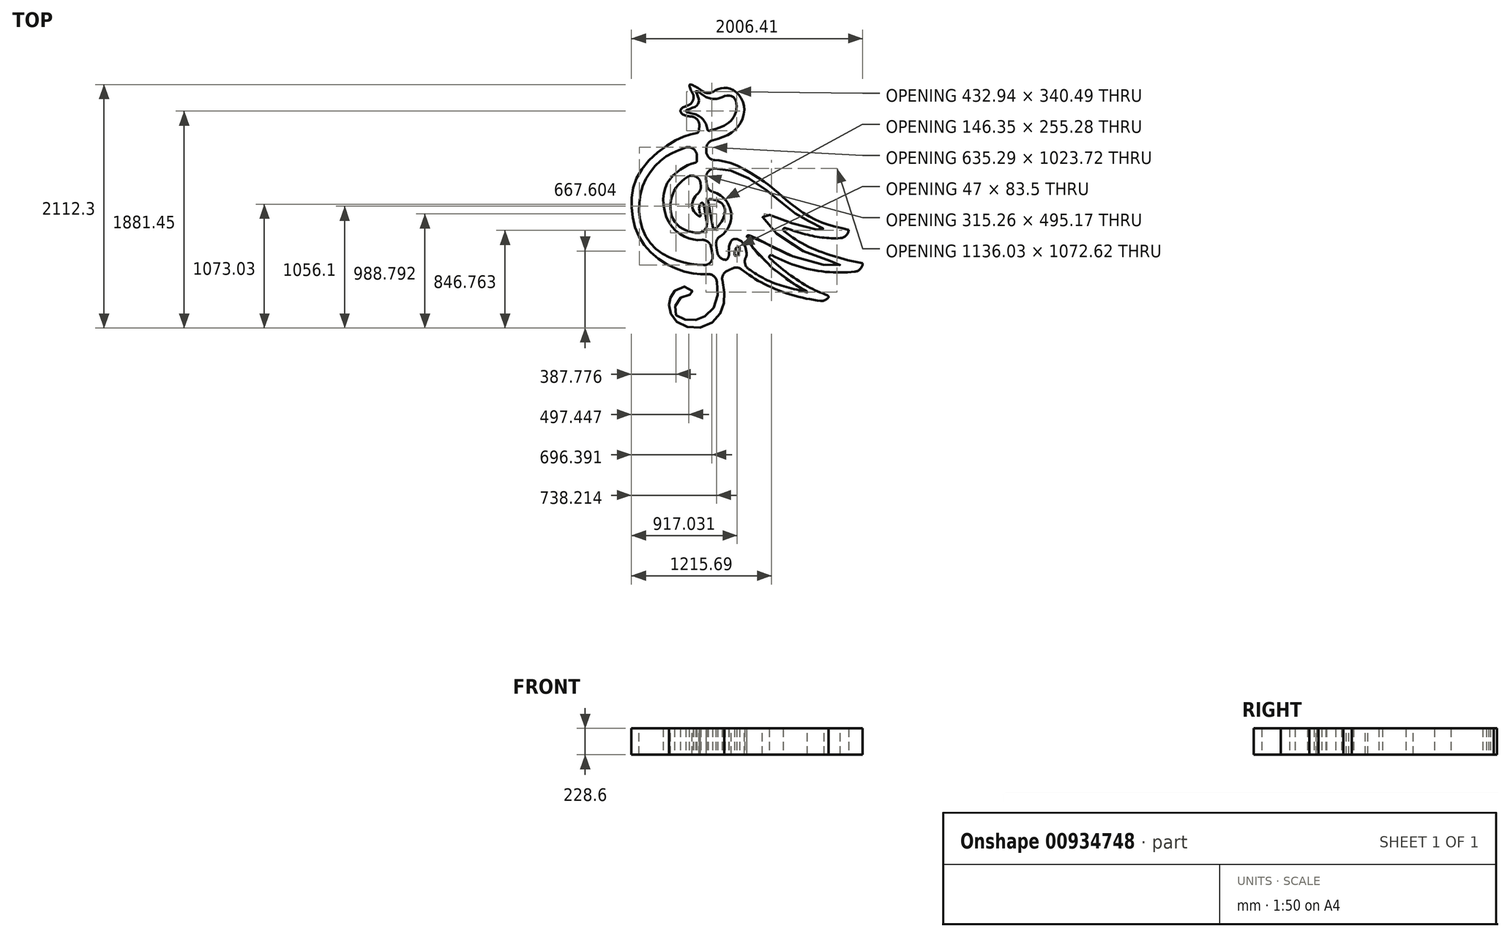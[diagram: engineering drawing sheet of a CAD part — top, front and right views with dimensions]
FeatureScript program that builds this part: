
annotation { "Feature Type Name" : "Feature", "Feature Type Description" : "" }
export const myFeature = defineFeature(function(context is Context, id is Id, definition is map)
    precondition{}
    {
        {
            var Q0;
            Q0=qCreatedBy(makeId("Top.planeOp"),FACE);
            var sketch = newSketch(context, id + "F0", { "sketchPlane" : qUnion([Q0])});
            skFitSpline(sketch, "E0", {"points": [v(-10.13, 34.53) * mm, v(-7.21, 36.28) * mm, v(-3.57, 36.28) * mm, v(0, 32.05) * mm, v(-1.82, 25.06) * mm, v(-10.75, 21.03) * mm], "startDerivative": vector(17.87, 13.15) * mm, "endDerivative": vector(-40.47, -9.18) * mm});
            skLineSegment(sketch, "E1", {"start": v(-10.75, 21.03) * mm, "end": v(-10.75, 15.74) * mm});
            skFitSpline(sketch, "E2", {"points": [v(-10.75, 15.74) * mm, v(-9.04, 15.74) * mm, v(-3.73, 14.85) * mm, v(7.09, 8.67) * mm, v(12.2, 4.3) * mm, v(20.6, -1.41) * mm, v(30.4, -4.44) * mm], "startDerivative": vector(20.65, 0.25) * mm, "endDerivative": vector(50.35, -11.32) * mm});
            skFitSpline(sketch, "E3", {"points": [v(30.4, -4.44) * mm, v(31.48, -5.44) * mm, v(31.42, -6.46) * mm], "startDerivative": vector(2.53, -1.73) * mm, "endDerivative": vector(-0.8, -2.05) * mm});
            skFitSpline(sketch, "E4", {"points": [v(31.42, -6.46) * mm, v(21.27, -6.46) * mm, v(9.3, -3) * mm], "startDerivative": vector(-21.03, -3.5) * mm, "endDerivative": vector(-23.27, 7.73) * mm});
            skFitSpline(sketch, "E5", {"points": [v(9.3, -3) * mm, v(16.48, -8.1) * mm, v(25.06, -11.75) * mm, v(34.46, -14.13) * mm], "startDerivative": vector(21.36, -16.71) * mm, "endDerivative": vector(26.92, -4.42) * mm});
            skFitSpline(sketch, "E6", {"points": [v(34.46, -14.13) * mm, v(35.57, -15.05) * mm, v(35.7, -16.2) * mm], "startDerivative": vector(2.6, -1.56) * mm, "endDerivative": vector(-0.18, -2.61) * mm});
            skFitSpline(sketch, "E7", {"points": [v(35.7, -16.2) * mm, v(25.95, -16.75) * mm, v(14.56, -14.62) * mm, v(5.06, -10.17) * mm], "startDerivative": vector(-29.63, -3.24) * mm, "endDerivative": vector(-27.45, 14.78) * mm});
            skFitSpline(sketch, "E8", {"points": [v(5.06, -10.17) * mm, v(10.3, -15.05) * mm, v(18.4, -20.71) * mm, v(24.86, -23.63) * mm], "startDerivative": vector(15.22, -15.1) * mm, "endDerivative": vector(19.9, -7.85) * mm});
            skFitSpline(sketch, "E9", {"points": [v(24.86, -23.63) * mm, v(25.6, -24.34) * mm, v(25.86, -25.36) * mm], "startDerivative": vector(1.72, -1.28) * mm, "endDerivative": vector(0.3, -2.17) * mm});
            skFitSpline(sketch, "E10", {"points": [v(25.86, -25.36) * mm, v(16.25, -23.9) * mm, v(4.88, -19.52) * mm, v(-1.94, -14.8) * mm], "startDerivative": vector(-28.22, 2.8) * mm, "endDerivative": vector(-20.3, 15.93) * mm});
            skFitSpline(sketch, "E11", {"points": [v(-1.94, -14.8) * mm, v(-4.07, -16.02) * mm, v(-6.53, -16.82) * mm], "startDerivative": vector(-4.2, -2.68) * mm, "endDerivative": vector(-5, -1.36) * mm});
            skFitSpline(sketch, "E12", {"points": [v(-6.53, -16.82) * mm, v(-5.58, -22.99) * mm, v(-6.12, -27.34) * mm, v(-9.82, -31.79) * mm, v(-16.34, -32.55) * mm, v(-20.41, -29.82) * mm, v(-21.58, -26.53) * mm, v(-21.26, -24.33) * mm, v(-19.8, -22.06) * mm, v(-16.12, -21) * mm, v(-14.63, -22.91) * mm, v(-16.73, -23.3) * mm, v(-19.49, -25.89) * mm, v(-19.42, -29.22) * mm, v(-15.27, -30.57) * mm, v(-11.66, -29.72) * mm, v(-7.87, -25.36) * mm, v(-7.8, -18.66) * mm, v(-7.97, -16.82) * mm], "startDerivative": vector(17.62, -92.77) * mm, "endDerivative": vector(-2.9, 39.27) * mm});
            skFitSpline(sketch, "E13", {"points": [v(-7.97, -16.82) * mm, v(-11.92, -17.32) * mm, v(-20.1, -15.42) * mm, v(-28.9, -8.64) * mm, v(-32.39, 1.98) * mm, v(-29.53, 12.97) * mm, v(-18.95, 21.78) * mm, v(-13.06, 23.63) * mm], "startDerivative": vector(-38.08, -8.2) * mm, "endDerivative": vector(45.84, 9.25) * mm});
            skLineSegment(sketch, "E14", {"start": v(-13.06, 23.63) * mm, "end": v(-12.39, 28.22) * mm});
            skFitSpline(sketch, "E15", {"points": [v(-13.01, 32.27) * mm, v(-15.6, 37.51) * mm, v(-10.13, 34.53) * mm], "startDerivative": vector(-9.2, 14.72) * mm, "endDerivative": vector(14.84, -10.07) * mm});
            skFitSpline(sketch, "E16", {"points": [v(-12.39, 28.22) * mm, v(-17.63, 29) * mm, v(-18.11, 30.39) * mm, v(-13.01, 32.27) * mm], "startDerivative": vector(-16.14, 0.23) * mm, "endDerivative": vector(17.28, 3.78) * mm});
            skFitSpline(sketch, "E17", {"points": [v(-11.13, 13.07) * mm, v(-4.51, 12.94) * mm, v(5.07, 8.13) * mm, v(13.22, 1.65) * mm, v(18.4, -1.77) * mm, v(23.3, -4.37) * mm, v(15.18, -2.91) * mm, v(5.48, 0) * mm, v(14.91, -9.33) * mm, v(28, -14.5) * mm, v(16.18, -12.87) * mm, v(1.1, -6.15) * mm, v(9.12, -16.25) * mm, v(18.48, -22.46) * mm, v(8.38, -19.25) * mm], "startDerivative": vector(111.68, 10.83) * mm, "endDerivative": vector(-207.34, 71.55) * mm});
            skFitSpline(sketch, "E18", {"points": [v(18.48, -22.46) * mm, v(7.51, -19.32) * mm, v(-0.84, -14.12) * mm], "startDerivative": vector(-22.14, 4.82) * mm, "endDerivative": vector(-16.43, 11.95) * mm});
            skFitSpline(sketch, "E19", {"points": [v(-0.84, -14.12) * mm, v(0.6, -12.65) * mm, v(0.59, -9.6) * mm, v(-1.32, -7.34) * mm, v(-3.45, -7.55) * mm, v(-4.2, -10.99) * mm, v(-3.45, -12.62) * mm], "startDerivative": vector(11.39, 8.05) * mm, "endDerivative": vector(6.68, -9.48) * mm});
            skLineSegment(sketch, "E20", {"start": v(-3.45, -12.62) * mm, "end": v(-7.02, -14.28) * mm});
            skLineSegment(sketch, "E21", {"start": v(-7.02, -14.28) * mm, "end": v(-8.25, -6.85) * mm});
            skFitSpline(sketch, "E22", {"points": [v(-1.3, -9.18) * mm, v(-2.5, -10.5) * mm, v(-2.38, -11.97) * mm, v(-1.29, -10.94) * mm, v(-1.3, -9.18) * mm]});
            skLineSegment(sketch, "E23", {"start": v(-11.13, 13.07) * mm, "end": v(-10.41, 6.9) * mm});
            skFitSpline(sketch, "E24", {"points": [v(-10.41, 6.9) * mm, v(-6.43, 5.3) * mm, v(-3.53, 0) * mm, v(-5.67, -5.52) * mm, v(-8.25, -6.85) * mm], "startDerivative": vector(17.17, -4.04) * mm, "endDerivative": vector(-13.43, -4.01) * mm});
            skLineSegment(sketch, "E25", {"start": v(-13.46, 20.4) * mm, "end": v(-13.46, 15.12) * mm});
            skLineSegment(sketch, "E26", {"start": v(-12.9, 12.8) * mm, "end": v(-12.13, 6.7) * mm});
            skLineSegment(sketch, "E27", {"start": v(-11.64, 3.88) * mm, "end": v(-10.22, -4.8) * mm});
            skLineSegment(sketch, "E28", {"start": v(-9.84, -7.12) * mm, "end": v(-8.36, -14.68) * mm});
            skLineSegment(sketch, "E29", {"start": v(-10.35, 4.3) * mm, "end": v(-8.65, -4.54) * mm});
            skFitSpline(sketch, "E30", {"points": [v(-10.35, 4.3) * mm, v(-7.54, 3.94) * mm, v(-5.43, 1.87) * mm, v(-6.37, -2.14) * mm, v(-8.65, -4.54) * mm], "startDerivative": vector(13.48, 2.7) * mm, "endDerivative": vector(-9.9, -7.5) * mm});
            skFitSpline(sketch, "E31", {"points": [v(-10.22, -4.8) * mm, v(-13.77, -5.29) * mm, v(-19.92, -2.13) * mm, v(-20.51, 5.76) * mm, v(-16.7, 10.53) * mm, v(-12.9, 12.8) * mm], "startDerivative": vector(-19.94, -5.82) * mm, "endDerivative": vector(21.4, 11.25) * mm});
            skFitSpline(sketch, "E32", {"points": [v(-9.84, -7.12) * mm, v(-15.2, -7.12) * mm, v(-21.65, -2.14) * mm, v(-22.66, 7.61) * mm, v(-18.38, 12.9) * mm, v(-13.46, 15.12) * mm], "startDerivative": vector(-29.72, -3.95) * mm, "endDerivative": vector(28.59, 4.89) * mm});
            skFitSpline(sketch, "E33", {"points": [v(-13.46, 20.4) * mm, v(-22.96, 16.34) * mm, v(-29.72, 6.27) * mm, v(-27.32, -7.8) * mm, v(-16.73, -14.02) * mm, v(-8.36, -14.68) * mm], "startDerivative": vector(-54.3, -17.43) * mm, "endDerivative": vector(46.52, 1.31) * mm});
            skFitSpline(sketch, "E34", {"points": [v(-11.64, 3.88) * mm, v(-12.86, 1.87) * mm, v(-12.45, -0.54) * mm, v(-14.45, 1.05) * mm, v(-14.45, 4.38) * mm, v(-12.13, 6.7) * mm], "startDerivative": vector(-9.9, -9.04) * mm, "endDerivative": vector(15.08, 6.28) * mm});
            skLineSegment(sketch, "E35", {"start": v(-12.54, 34.42) * mm, "end": v(-8.5, 32.11) * mm});
            skLineSegment(sketch, "E36", {"start": v(-12.54, 34.42) * mm, "end": v(-10.37, 30.67) * mm});
            skLineSegment(sketch, "E37", {"start": v(-10.37, 30.67) * mm, "end": v(-12.25, 30.1) * mm});
            skLineSegment(sketch, "E38", {"start": v(-12.25, 30.1) * mm, "end": v(-9.99, 28.4) * mm});
            skLineSegment(sketch, "E39", {"start": v(-9.99, 28.4) * mm, "end": v(-10.56, 24.03) * mm});
            skFitSpline(sketch, "E40", {"points": [v(-10.56, 24.03) * mm, v(-5.03, 26) * mm, v(-2.38, 29.08) * mm, v(-2.48, 33.36) * mm, v(-5.03, 34.37) * mm, v(-8.5, 32.11) * mm], "startDerivative": vector(25.42, 6.86) * mm, "endDerivative": vector(-17, -15.34) * mm});
            skLineSegment(sketch, "E41", {"start": v(-36.5, 0) * mm, "end": v(39.7, 0) * mm, "construction": true});
            skSolve(sketch);
        }
        {
            var Q0;
            Q0 = qSketchRegion(id + "F0", true);
            extrude(context, id + "F1", {"entities" : qUnion([Q0]), "depth" : 7.62 * mm, "offsetDistance" : 25.4 * mm});
        }
        {
            var Q0;
            Q0=makeQuery(id+"F1.opExtrude","SWEPT_EDGE",EDGE,{"disambiguationData":[OSD([sQuery(id+"F0.wireOp",EDGE,"E0"),sQuery(id+"F0.wireOp",EDGE,"E1")])]});
            var Q1;
            Q1=makeQuery(id+"F1.opExtrude","SWEPT_EDGE",EDGE,{"disambiguationData":[OSD([sQuery(id+"F0.wireOp",EDGE,"E1"),sQuery(id+"F0.wireOp",EDGE,"E2")])]});
            var Q2;
            Q2=makeQuery(id+"F1.opExtrude","SWEPT_EDGE",EDGE,{"disambiguationData":[OSD([sQuery(id+"F0.wireOp",EDGE,"E3"),sQuery(id+"F0.wireOp",EDGE,"E4")])]});
            var Q3;
            Q3=makeQuery(id+"F1.opExtrude","SWEPT_EDGE",EDGE,{"disambiguationData":[OSD([sQuery(id+"F0.wireOp",EDGE,"E6"),sQuery(id+"F0.wireOp",EDGE,"E7")])]});
            var Q4;
            Q4=makeQuery(id+"F1.opExtrude","SWEPT_EDGE",EDGE,{"disambiguationData":[OSD([sQuery(id+"F0.wireOp",EDGE,"E9"),sQuery(id+"F0.wireOp",EDGE,"E10")])]});
            var Q5;
            Q5=makeQuery(id+"F1.opExtrude","SWEPT_EDGE",EDGE,{"disambiguationData":[OSD([sQuery(id+"F0.wireOp",EDGE,"E11"),sQuery(id+"F0.wireOp",EDGE,"E12")])]});
            var Q6;
            Q6=makeQuery(id+"F1.opExtrude","SWEPT_EDGE",EDGE,{"disambiguationData":[OSD([sQuery(id+"F0.wireOp",EDGE,"E10"),sQuery(id+"F0.wireOp",EDGE,"E11")])]});
            var Q7;
            Q7=makeQuery(id+"F1.opExtrude","SWEPT_EDGE",EDGE,{"disambiguationData":[OSD([sQuery(id+"F0.wireOp",EDGE,"E18"),sQuery(id+"F0.wireOp",EDGE,"E19")])]});
            var Q8;
            Q8=makeQuery(id+"F1.opExtrude","SWEPT_EDGE",EDGE,{"disambiguationData":[OSD([sQuery(id+"F0.wireOp",EDGE,"E20"),sQuery(id+"F0.wireOp",EDGE,"E21")])]});
            var Q9;
            Q9=makeQuery(id+"F1.opExtrude","SWEPT_EDGE",EDGE,{"disambiguationData":[OSD([sQuery(id+"F0.wireOp",EDGE,"E19"),sQuery(id+"F0.wireOp",EDGE,"E20")])]});
            var Q10;
            Q10=makeQuery(id+"F1.opExtrude","SWEPT_EDGE",EDGE,{"disambiguationData":[OSD([sQuery(id+"F0.wireOp",EDGE,"E21"),sQuery(id+"F0.wireOp",EDGE,"E24")])]});
            var Q11;
            Q11=makeQuery(id+"F1.opExtrude","SWEPT_EDGE",EDGE,{"disambiguationData":[OSD([sQuery(id+"F0.wireOp",EDGE,"E12"),sQuery(id+"F0.wireOp",EDGE,"E13")])]});
            var Q12;
            Q12=makeQuery(id+"F1.opExtrude","SWEPT_EDGE",EDGE,{"disambiguationData":[OSD([sQuery(id+"F0.wireOp",EDGE,"E28"),sQuery(id+"F0.wireOp",EDGE,"E32")])]});
            var Q13;
            Q13=makeQuery(id+"F1.opExtrude","SWEPT_EDGE",EDGE,{"disambiguationData":[OSD([sQuery(id+"F0.wireOp",EDGE,"E28"),sQuery(id+"F0.wireOp",EDGE,"E33")])]});
            var Q14;
            Q14=makeQuery(id+"F1.opExtrude","SWEPT_EDGE",EDGE,{"disambiguationData":[OSD([sQuery(id+"F0.wireOp",EDGE,"E17"),sQuery(id+"F0.wireOp",EDGE,"E23")])]});
            var Q15;
            Q15=makeQuery(id+"F1.opExtrude","SWEPT_EDGE",EDGE,{"disambiguationData":[OSD([sQuery(id+"F0.wireOp",EDGE,"E26"),sQuery(id+"F0.wireOp",EDGE,"E31")])]});
            var Q16;
            Q16=makeQuery(id+"F1.opExtrude","SWEPT_EDGE",EDGE,{"disambiguationData":[OSD([sQuery(id+"F0.wireOp",EDGE,"E25"),sQuery(id+"F0.wireOp",EDGE,"E33")])]});
            var Q17;
            Q17=makeQuery(id+"F1.opExtrude","SWEPT_EDGE",EDGE,{"disambiguationData":[OSD([sQuery(id+"F0.wireOp",EDGE,"E14"),sQuery(id+"F0.wireOp",EDGE,"E16")])]});
            var Q18;
            Q18=makeQuery(id+"F1.opExtrude","SWEPT_EDGE",EDGE,{"disambiguationData":[OSD([sQuery(id+"F0.wireOp",EDGE,"E15"),sQuery(id+"F0.wireOp",EDGE,"E16")])]});
            var Q19;
            Q19=makeQuery(id+"F1.opExtrude","SWEPT_EDGE",EDGE,{"disambiguationData":[OSD([sQuery(id+"F0.wireOp",EDGE,"E0"),sQuery(id+"F0.wireOp",EDGE,"E15")])]});
            var Q20;
            Q20=makeQuery(id+"F1.opExtrude","SWEPT_EDGE",EDGE,{"disambiguationData":[OSD([sQuery(id+"F0.wireOp",EDGE,"E27"),sQuery(id+"F0.wireOp",EDGE,"E31")])]});
            var Q21;
            Q21=makeQuery(id+"F1.opExtrude","SWEPT_EDGE",EDGE,{"disambiguationData":[OSD([sQuery(id+"F0.wireOp",EDGE,"E26"),sQuery(id+"F0.wireOp",EDGE,"E34")])]});
            var Q22;
            Q22=makeQuery(id+"F1.opExtrude","SWEPT_EDGE",EDGE,{"disambiguationData":[OSD([sQuery(id+"F0.wireOp",EDGE,"E23"),sQuery(id+"F0.wireOp",EDGE,"E24")])]});
            fillet(context, id + "F2", {"entities" : qUnion([Q0, Q1, Q2, Q3, Q4, Q5, Q6, Q7, Q8, Q9, Q10, Q11, Q12, Q13, Q14, Q15, Q16, Q17, Q18, Q19, Q20, Q21, Q22]), "radius" : 2.54 * mm, "tangentPropagation" : true, "allowEdgeOverflow" : false});
        }
        {
            var Q0;
            Q0=makeQuery(id+"F1.opExtrude","SWEPT_EDGE",EDGE,{"disambiguationData":[OSD([sQuery(id+"F0.wireOp",EDGE,"E35"),sQuery(id+"F0.wireOp",EDGE,"E40")])]});
            var Q1;
            Q1=makeQuery(id+"F1.opExtrude","SWEPT_EDGE",EDGE,{"disambiguationData":[OSD([sQuery(id+"F0.wireOp",EDGE,"E35"),sQuery(id+"F0.wireOp",EDGE,"E36")])]});
            var Q2;
            Q2=makeQuery(id+"F1.opExtrude","SWEPT_EDGE",EDGE,{"disambiguationData":[OSD([sQuery(id+"F0.wireOp",EDGE,"E36"),sQuery(id+"F0.wireOp",EDGE,"E37")])]});
            var Q3;
            Q3=makeQuery(id+"F1.opExtrude","SWEPT_EDGE",EDGE,{"disambiguationData":[OSD([sQuery(id+"F0.wireOp",EDGE,"E37"),sQuery(id+"F0.wireOp",EDGE,"E38")])]});
            var Q4;
            Q4=makeQuery(id+"F1.opExtrude","SWEPT_EDGE",EDGE,{"disambiguationData":[OSD([sQuery(id+"F0.wireOp",EDGE,"E38"),sQuery(id+"F0.wireOp",EDGE,"E39")])]});
            var Q5;
            Q5=makeQuery(id+"F1.opExtrude","SWEPT_EDGE",EDGE,{"disambiguationData":[OSD([sQuery(id+"F0.wireOp",EDGE,"E39"),sQuery(id+"F0.wireOp",EDGE,"E40")])]});
            var Q6;
            Q6=makeQuery(id+"F1.opExtrude","SWEPT_EDGE",EDGE,{"disambiguationData":[OSD([sQuery(id+"F0.wireOp",EDGE,"E13"),sQuery(id+"F0.wireOp",EDGE,"E14")])]});
            var Q7;
            Q7=makeQuery(id+"F1.opExtrude","SWEPT_EDGE",EDGE,{"disambiguationData":[OSD([sQuery(id+"F0.wireOp",EDGE,"E25"),sQuery(id+"F0.wireOp",EDGE,"E32")])]});
            var Q8;
            Q8=makeQuery(id+"F1.opExtrude","SWEPT_EDGE",EDGE,{"disambiguationData":[OSD([sQuery(id+"F0.wireOp",EDGE,"E27"),sQuery(id+"F0.wireOp",EDGE,"E34")])]});
            var Q9;
            {var subQ0=sQuery(id+"F0.wireOp",EDGE,"E30");var subQ1=sQuery(id+"F0.wireOp",EDGE,"E29");Q9=makeQuery(id+"F1.opExtrude","SWEPT_EDGE",EDGE,{"disambiguationData":[OSD([subQ1,subQ0]),TDD([makeQuery(id+"F0.imprint","INTERSECT",VERTEX,{"disambiguationData":[OD(0.0)],"derivedFrom":[subQ1,subQ0]})])]});}
            var Q10;
            {var subQ0=sQuery(id+"F0.wireOp",EDGE,"E30");var subQ1=sQuery(id+"F0.wireOp",EDGE,"E29");Q10=makeQuery(id+"F1.opExtrude","SWEPT_EDGE",EDGE,{"disambiguationData":[OSD([subQ1,subQ0]),TDD([makeQuery(id+"F0.imprint","INTERSECT",VERTEX,{"disambiguationData":[OD(1.0)],"derivedFrom":[subQ1,subQ0]})])]});}
            var Q11;
            Q11=makeQuery(id+"F1.opExtrude","SWEPT_EDGE",EDGE,{"disambiguationData":[OSD([sQuery(id+"F0.wireOp",EDGE,"E4"),sQuery(id+"F0.wireOp",EDGE,"E5")])]});
            var Q12;
            Q12=makeQuery(id+"F1.opExtrude","SWEPT_EDGE",EDGE,{"disambiguationData":[OSD([sQuery(id+"F0.wireOp",EDGE,"E7"),sQuery(id+"F0.wireOp",EDGE,"E8")])]});
            var Q13;
            Q13=makeQuery(id+"F2.opFillet","BLEND_EDGE",EDGE,{"blendedFrom":[makeQuery(id+"F1.opExtrude","SWEPT_EDGE",EDGE,{"disambiguationData":[OSD([sQuery(id+"F0.wireOp",EDGE,"E9"),sQuery(id+"F0.wireOp",EDGE,"E10")])]}),makeQuery(id+"F1.opExtrude","SWEPT_FACE",FACE,{"disambiguationData":[OSD([sQuery(id+"F0.wireOp",EDGE,"E8")])]})],"blendedInto":[makeQuery(id+"F1.opExtrude","SWEPT_FACE",FACE,{"disambiguationData":[OSD([sQuery(id+"F0.wireOp",EDGE,"E8")])]})]});
            var Q14;
            Q14=makeQuery(id+"F1.opExtrude","SWEPT_EDGE",EDGE,{"disambiguationData":[OSD([sQuery(id+"F0.wireOp",EDGE,"E17"),sQuery(id+"F0.wireOp",EDGE,"E18")])]});
            var Q15;
            {var subQ0=sQuery(id+"F0.wireOp",EDGE,"E20");Q15=makeQuery(id+"F2.opFillet","BLEND_EDGE",EDGE,{"blendedFrom":[makeQuery(id+"F1.opExtrude","SWEPT_EDGE",EDGE,{"disambiguationData":[OSD([sQuery(id+"F0.wireOp",EDGE,"E19"),subQ0])]}),makeQuery(id+"F1.opExtrude","SWEPT_EDGE",EDGE,{"disambiguationData":[OSD([subQ0,sQuery(id+"F0.wireOp",EDGE,"E21")])]})],"blendedInto":[]});}
            fillet(context, id + "F3", {"entities" : qUnion([Q0, Q1, Q2, Q3, Q4, Q5, Q6, Q7, Q8, Q9, Q10, Q11, Q12, Q13, Q14, Q15]), "radius" : 0.5 * mm, "tangentPropagation" : true, "allowEdgeOverflow" : false});
        }
        {
            var Q0;
            Q0=makeQuery(id+"F1.opExtrude","CAP_FACE",FACE,{"disambiguationData":[OSD([sQuery(id+"F0.wireOp",EDGE,"E0"),sQuery(id+"F0.wireOp",EDGE,"E1"),sQuery(id+"F0.wireOp",EDGE,"E2"),sQuery(id+"F0.wireOp",EDGE,"E3"),sQuery(id+"F0.wireOp",EDGE,"E4"),sQuery(id+"F0.wireOp",EDGE,"E5"),sQuery(id+"F0.wireOp",EDGE,"E6"),sQuery(id+"F0.wireOp",EDGE,"E7"),sQuery(id+"F0.wireOp",EDGE,"E8"),sQuery(id+"F0.wireOp",EDGE,"E9"),sQuery(id+"F0.wireOp",EDGE,"E10"),sQuery(id+"F0.wireOp",EDGE,"E11"),sQuery(id+"F0.wireOp",EDGE,"E12"),sQuery(id+"F0.wireOp",EDGE,"E13"),sQuery(id+"F0.wireOp",EDGE,"E14"),sQuery(id+"F0.wireOp",EDGE,"E15"),sQuery(id+"F0.wireOp",EDGE,"E16"),sQuery(id+"F0.wireOp",EDGE,"E17"),sQuery(id+"F0.wireOp",EDGE,"E18"),sQuery(id+"F0.wireOp",EDGE,"E19"),sQuery(id+"F0.wireOp",EDGE,"E20"),sQuery(id+"F0.wireOp",EDGE,"E21"),sQuery(id+"F0.wireOp",EDGE,"E22"),sQuery(id+"F0.wireOp",EDGE,"E23"),sQuery(id+"F0.wireOp",EDGE,"E24"),sQuery(id+"F0.wireOp",EDGE,"E25"),sQuery(id+"F0.wireOp",EDGE,"E26"),sQuery(id+"F0.wireOp",EDGE,"E27"),sQuery(id+"F0.wireOp",EDGE,"E28"),sQuery(id+"F0.wireOp",EDGE,"E29"),sQuery(id+"F0.wireOp",EDGE,"E30"),sQuery(id+"F0.wireOp",EDGE,"E31"),sQuery(id+"F0.wireOp",EDGE,"E32"),sQuery(id+"F0.wireOp",EDGE,"E33"),sQuery(id+"F0.wireOp",EDGE,"E34"),sQuery(id+"F0.wireOp",EDGE,"E35"),sQuery(id+"F0.wireOp",EDGE,"E36"),sQuery(id+"F0.wireOp",EDGE,"E37"),sQuery(id+"F0.wireOp",EDGE,"E38"),sQuery(id+"F0.wireOp",EDGE,"E39"),sQuery(id+"F0.wireOp",EDGE,"E40")])],"isStart":false});
            var sketch = newSketch(context, id + "F4", { "sketchPlane" : qUnion([Q0])});
            skFitSpline(sketch, "E42", {"points": [v(-8.81, 32.3) * mm, v(-13.75, 35.61) * mm, v(-12.99, 33.57) * mm, v(-13.89, 31.24) * mm, v(-16.63, 29.94) * mm, v(-10.02, 28.11) * mm], "startDerivative": vector(-26.98, 22.72) * mm, "endDerivative": vector(33.51, -7.9) * mm});
            skLineSegment(sketch, "E43", {"start": v(-10.02, 28.11) * mm, "end": v(-8.81, 32.3) * mm});
            skSolve(sketch);
        }
        {
            var Q0;
            Q0 = qSketchRegion(id + "F4", true);
            extrude(context, id + "F5", {"entities" : qUnion([Q0]), "operationType" : NewBodyOperationType.REMOVE, "oppositeDirection" : true, "depth" : 25.4 * mm, "offsetDistance" : 25.4 * mm});
        }
        {
            var Q0;
            {var subQ0=sQuery(id+"F4.wireOp",EDGE,"E43");var subQ1=sQuery(id+"F4.wireOp",EDGE,"E42");var subQ2=sQuery(id+"F0.wireOp",EDGE,"E39");var subQ3=sQuery(id+"F0.wireOp",EDGE,"E40");var subQ4=sQuery(id+"F0.wireOp",EDGE,"E38");var subQ5=sQuery(id+"F0.wireOp",EDGE,"E37");var subQ6=sQuery(id+"F0.wireOp",EDGE,"E36");var subQ7=sQuery(id+"F0.wireOp",EDGE,"E35");var subQ8=sQuery(id+"F0.wireOp",EDGE,"E34");var subQ9=sQuery(id+"F0.wireOp",EDGE,"E33");var subQ10=sQuery(id+"F0.wireOp",EDGE,"E32");var subQ11=sQuery(id+"F0.wireOp",EDGE,"E31");var subQ12=sQuery(id+"F0.wireOp",EDGE,"E30");var subQ13=sQuery(id+"F0.wireOp",EDGE,"E29");var subQ14=sQuery(id+"F0.wireOp",EDGE,"E28");var subQ15=sQuery(id+"F0.wireOp",EDGE,"E27");var subQ16=sQuery(id+"F0.wireOp",EDGE,"E26");var subQ17=sQuery(id+"F0.wireOp",EDGE,"E25");var subQ18=sQuery(id+"F0.wireOp",EDGE,"E24");var subQ19=sQuery(id+"F0.wireOp",EDGE,"E23");var subQ20=sQuery(id+"F0.wireOp",EDGE,"E22");var subQ21=sQuery(id+"F0.wireOp",EDGE,"E21");var subQ22=sQuery(id+"F0.wireOp",EDGE,"E20");var subQ23=sQuery(id+"F0.wireOp",EDGE,"E19");var subQ24=sQuery(id+"F0.wireOp",EDGE,"E18");var subQ25=sQuery(id+"F0.wireOp",EDGE,"E17");var subQ26=sQuery(id+"F0.wireOp",EDGE,"E16");var subQ27=sQuery(id+"F0.wireOp",EDGE,"E15");var subQ28=sQuery(id+"F0.wireOp",EDGE,"E14");var subQ29=sQuery(id+"F0.wireOp",EDGE,"E13");var subQ30=sQuery(id+"F0.wireOp",EDGE,"E12");var subQ31=sQuery(id+"F0.wireOp",EDGE,"E11");var subQ32=sQuery(id+"F0.wireOp",EDGE,"E10");var subQ33=sQuery(id+"F0.wireOp",EDGE,"E9");var subQ34=sQuery(id+"F0.wireOp",EDGE,"E8");var subQ35=sQuery(id+"F0.wireOp",EDGE,"E7");var subQ36=sQuery(id+"F0.wireOp",EDGE,"E6");var subQ37=sQuery(id+"F0.wireOp",EDGE,"E5");var subQ38=sQuery(id+"F0.wireOp",EDGE,"E4");var subQ39=sQuery(id+"F0.wireOp",EDGE,"E3");var subQ40=sQuery(id+"F0.wireOp",EDGE,"E2");var subQ41=sQuery(id+"F0.wireOp",EDGE,"E1");var subQ42=sQuery(id+"F0.wireOp",EDGE,"E0");var subQ43=makeQuery(id+"F1.opExtrude","SWEPT_EDGE",EDGE,{"disambiguationData":[OSD([subQ4,subQ2])]});Q0=makeQuery(id+"F5.boolean.opBoolean","MERGE",EDGE,{"derivedFrom":[makeQuery(id+"F3.opFillet","BLEND_EDGE",EDGE,{"blendedFrom":[subQ43,makeQuery(id+"F1.opExtrude","SWEPT_FACE",FACE,{"disambiguationData":[OSD([subQ2])]})],"blendedInto":[makeQuery(id+"F1.opExtrude","SWEPT_FACE",FACE,{"disambiguationData":[OSD([subQ2])]})]})],"fromTools":[makeQuery(id+"F5.opExtrude","SWEPT_EDGE",EDGE,{"disambiguationData":[OSD([subQ42,subQ41,subQ40,subQ39,subQ38,subQ37,subQ36,subQ35,subQ34,subQ33,subQ32,subQ31,subQ30,subQ29,subQ28,subQ27,subQ26,subQ25,subQ24,subQ23,subQ22,subQ21,subQ20,subQ19,subQ18,subQ17,subQ16,subQ15,subQ14,subQ13,subQ12,subQ11,subQ10,subQ9,subQ8,subQ7,subQ6,subQ5,subQ4,subQ2,subQ3,subQ1,subQ0]),TDD([makeQuery(id+"F4.imprint","INTERSECT",VERTEX,{"derivedFrom":[makeQuery(id+"F3.opFillet","BLEND_EDGE",EDGE,{"blendedFrom":[subQ43,makeQuery(id+"F1.opExtrude","CAP_FACE",FACE,{"disambiguationData":[OSD([subQ42,subQ41,subQ40,subQ39,subQ38,subQ37,subQ36,subQ35,subQ34,subQ33,subQ32,subQ31,subQ30,subQ29,subQ28,subQ27,subQ26,subQ25,subQ24,subQ23,subQ22,subQ21,subQ20,subQ19,subQ18,subQ17,subQ16,subQ15,subQ14,subQ13,subQ12,subQ11,subQ10,subQ9,subQ8,subQ7,subQ6,subQ5,subQ4,subQ2,subQ3])],"isStart":false})],"blendedInto":[makeQuery(id+"F1.opExtrude","CAP_FACE",FACE,{"disambiguationData":[OSD([subQ42,subQ41,subQ40,subQ39,subQ38,subQ37,subQ36,subQ35,subQ34,subQ33,subQ32,subQ31,subQ30,subQ29,subQ28,subQ27,subQ26,subQ25,subQ24,subQ23,subQ22,subQ21,subQ20,subQ19,subQ18,subQ17,subQ16,subQ15,subQ14,subQ13,subQ12,subQ11,subQ10,subQ9,subQ8,subQ7,subQ6,subQ5,subQ4,subQ2,subQ3])],"isStart":false})]}),makeQuery(id+"F1.opExtrude","CAP_EDGE",EDGE,{"disambiguationData":[OSD([subQ2])],"isStart":false}),subQ1,subQ0]})])]})]});}
            var Q1;
            {var subQ0=sQuery(id+"F4.wireOp",EDGE,"E43");var subQ1=sQuery(id+"F4.wireOp",EDGE,"E42");var subQ2=sQuery(id+"F0.wireOp",EDGE,"E35");var subQ3=sQuery(id+"F0.wireOp",EDGE,"E40");var subQ4=sQuery(id+"F0.wireOp",EDGE,"E39");var subQ5=sQuery(id+"F0.wireOp",EDGE,"E38");var subQ6=sQuery(id+"F0.wireOp",EDGE,"E37");var subQ7=sQuery(id+"F0.wireOp",EDGE,"E36");var subQ8=sQuery(id+"F0.wireOp",EDGE,"E34");var subQ9=sQuery(id+"F0.wireOp",EDGE,"E33");var subQ10=sQuery(id+"F0.wireOp",EDGE,"E32");var subQ11=sQuery(id+"F0.wireOp",EDGE,"E31");var subQ12=sQuery(id+"F0.wireOp",EDGE,"E30");var subQ13=sQuery(id+"F0.wireOp",EDGE,"E29");var subQ14=sQuery(id+"F0.wireOp",EDGE,"E28");var subQ15=sQuery(id+"F0.wireOp",EDGE,"E27");var subQ16=sQuery(id+"F0.wireOp",EDGE,"E26");var subQ17=sQuery(id+"F0.wireOp",EDGE,"E25");var subQ18=sQuery(id+"F0.wireOp",EDGE,"E24");var subQ19=sQuery(id+"F0.wireOp",EDGE,"E23");var subQ20=sQuery(id+"F0.wireOp",EDGE,"E22");var subQ21=sQuery(id+"F0.wireOp",EDGE,"E21");var subQ22=sQuery(id+"F0.wireOp",EDGE,"E20");var subQ23=sQuery(id+"F0.wireOp",EDGE,"E19");var subQ24=sQuery(id+"F0.wireOp",EDGE,"E18");var subQ25=sQuery(id+"F0.wireOp",EDGE,"E17");var subQ26=sQuery(id+"F0.wireOp",EDGE,"E16");var subQ27=sQuery(id+"F0.wireOp",EDGE,"E15");var subQ28=sQuery(id+"F0.wireOp",EDGE,"E14");var subQ29=sQuery(id+"F0.wireOp",EDGE,"E13");var subQ30=sQuery(id+"F0.wireOp",EDGE,"E12");var subQ31=sQuery(id+"F0.wireOp",EDGE,"E11");var subQ32=sQuery(id+"F0.wireOp",EDGE,"E10");var subQ33=sQuery(id+"F0.wireOp",EDGE,"E9");var subQ34=sQuery(id+"F0.wireOp",EDGE,"E8");var subQ35=sQuery(id+"F0.wireOp",EDGE,"E7");var subQ36=sQuery(id+"F0.wireOp",EDGE,"E6");var subQ37=sQuery(id+"F0.wireOp",EDGE,"E5");var subQ38=sQuery(id+"F0.wireOp",EDGE,"E4");var subQ39=sQuery(id+"F0.wireOp",EDGE,"E3");var subQ40=sQuery(id+"F0.wireOp",EDGE,"E2");var subQ41=sQuery(id+"F0.wireOp",EDGE,"E1");var subQ42=sQuery(id+"F0.wireOp",EDGE,"E0");var subQ43=makeQuery(id+"F1.opExtrude","SWEPT_EDGE",EDGE,{"disambiguationData":[OSD([subQ2,subQ3])]});Q1=makeQuery(id+"F5.boolean.opBoolean","MERGE",EDGE,{"derivedFrom":[makeQuery(id+"F3.opFillet","BLEND_EDGE",EDGE,{"blendedFrom":[subQ43,makeQuery(id+"F1.opExtrude","SWEPT_FACE",FACE,{"disambiguationData":[OSD([subQ2])]})],"blendedInto":[makeQuery(id+"F1.opExtrude","SWEPT_FACE",FACE,{"disambiguationData":[OSD([subQ2])]})]})],"fromTools":[makeQuery(id+"F5.opExtrude","SWEPT_EDGE",EDGE,{"disambiguationData":[OSD([subQ42,subQ41,subQ40,subQ39,subQ38,subQ37,subQ36,subQ35,subQ34,subQ33,subQ32,subQ31,subQ30,subQ29,subQ28,subQ27,subQ26,subQ25,subQ24,subQ23,subQ22,subQ21,subQ20,subQ19,subQ18,subQ17,subQ16,subQ15,subQ14,subQ13,subQ12,subQ11,subQ10,subQ9,subQ8,subQ2,subQ7,subQ6,subQ5,subQ4,subQ3,subQ1,subQ0]),TDD([makeQuery(id+"F4.imprint","INTERSECT",VERTEX,{"derivedFrom":[makeQuery(id+"F3.opFillet","BLEND_EDGE",EDGE,{"blendedFrom":[subQ43,makeQuery(id+"F1.opExtrude","CAP_FACE",FACE,{"disambiguationData":[OSD([subQ42,subQ41,subQ40,subQ39,subQ38,subQ37,subQ36,subQ35,subQ34,subQ33,subQ32,subQ31,subQ30,subQ29,subQ28,subQ27,subQ26,subQ25,subQ24,subQ23,subQ22,subQ21,subQ20,subQ19,subQ18,subQ17,subQ16,subQ15,subQ14,subQ13,subQ12,subQ11,subQ10,subQ9,subQ8,subQ2,subQ7,subQ6,subQ5,subQ4,subQ3])],"isStart":false})],"blendedInto":[makeQuery(id+"F1.opExtrude","CAP_FACE",FACE,{"disambiguationData":[OSD([subQ42,subQ41,subQ40,subQ39,subQ38,subQ37,subQ36,subQ35,subQ34,subQ33,subQ32,subQ31,subQ30,subQ29,subQ28,subQ27,subQ26,subQ25,subQ24,subQ23,subQ22,subQ21,subQ20,subQ19,subQ18,subQ17,subQ16,subQ15,subQ14,subQ13,subQ12,subQ11,subQ10,subQ9,subQ8,subQ2,subQ7,subQ6,subQ5,subQ4,subQ3])],"isStart":false})]}),makeQuery(id+"F1.opExtrude","CAP_EDGE",EDGE,{"disambiguationData":[OSD([subQ2])],"isStart":false}),subQ1,subQ0]})])]})]});}
            fillet(context, id + "F6", {"entities" : qUnion([Q0, Q1]), "radius" : 5.08 * mm, "tangentPropagation" : true, "allowEdgeOverflow" : false});
        }
        {
            var Q0;
            Q0=makeQuery(id+"F1.opExtrude","SWEPT_BODY",BODY,{"disambiguationData":[OSD([sQuery(id+"F0.wireOp",EDGE,"E0"),sQuery(id+"F0.wireOp",EDGE,"E1"),sQuery(id+"F0.wireOp",EDGE,"E2"),sQuery(id+"F0.wireOp",EDGE,"E3"),sQuery(id+"F0.wireOp",EDGE,"E4"),sQuery(id+"F0.wireOp",EDGE,"E5"),sQuery(id+"F0.wireOp",EDGE,"E6"),sQuery(id+"F0.wireOp",EDGE,"E7"),sQuery(id+"F0.wireOp",EDGE,"E8"),sQuery(id+"F0.wireOp",EDGE,"E9"),sQuery(id+"F0.wireOp",EDGE,"E10"),sQuery(id+"F0.wireOp",EDGE,"E11"),sQuery(id+"F0.wireOp",EDGE,"E12"),sQuery(id+"F0.wireOp",EDGE,"E13"),sQuery(id+"F0.wireOp",EDGE,"E14"),sQuery(id+"F0.wireOp",EDGE,"E15"),sQuery(id+"F0.wireOp",EDGE,"E16"),sQuery(id+"F0.wireOp",EDGE,"E17"),sQuery(id+"F0.wireOp",EDGE,"E18"),sQuery(id+"F0.wireOp",EDGE,"E19"),sQuery(id+"F0.wireOp",EDGE,"E20"),sQuery(id+"F0.wireOp",EDGE,"E21"),sQuery(id+"F0.wireOp",EDGE,"E22"),sQuery(id+"F0.wireOp",EDGE,"E23"),sQuery(id+"F0.wireOp",EDGE,"E24"),sQuery(id+"F0.wireOp",EDGE,"E25"),sQuery(id+"F0.wireOp",EDGE,"E26"),sQuery(id+"F0.wireOp",EDGE,"E27"),sQuery(id+"F0.wireOp",EDGE,"E28"),sQuery(id+"F0.wireOp",EDGE,"E29"),sQuery(id+"F0.wireOp",EDGE,"E30"),sQuery(id+"F0.wireOp",EDGE,"E31"),sQuery(id+"F0.wireOp",EDGE,"E32"),sQuery(id+"F0.wireOp",EDGE,"E33"),sQuery(id+"F0.wireOp",EDGE,"E34"),sQuery(id+"F0.wireOp",EDGE,"E35"),sQuery(id+"F0.wireOp",EDGE,"E36"),sQuery(id+"F0.wireOp",EDGE,"E37"),sQuery(id+"F0.wireOp",EDGE,"E38"),sQuery(id+"F0.wireOp",EDGE,"E39"),sQuery(id+"F0.wireOp",EDGE,"E40")])]});
            var Q1;
            Q1=qCreatedBy(makeId("Origin.pointOp"),VERTEX);
            transform(context, id + "F7", {"entities" : qUnion([Q0]), "transformType" : TransformType.SCALE_UNIFORMLY, "scale" : 30, "scalePoint" : qUnion([Q1]), "makeCopy" : false});
        }
    });
